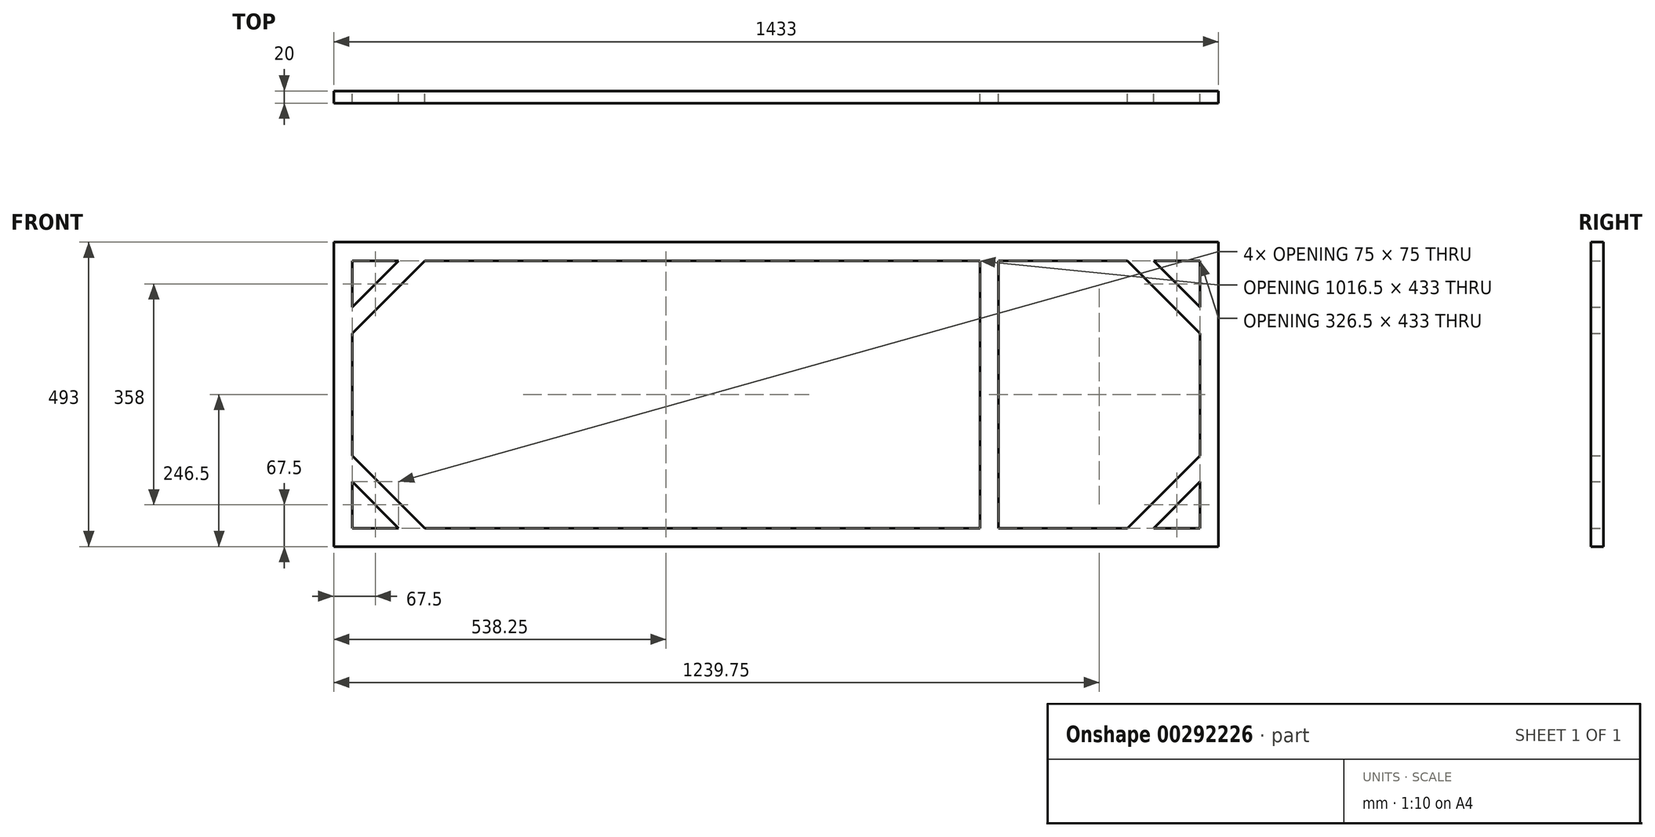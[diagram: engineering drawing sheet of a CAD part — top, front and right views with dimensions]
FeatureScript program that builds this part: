
annotation { "Feature Type Name" : "Feature", "Feature Type Description" : "" }
export const myFeature = defineFeature(function(context is Context, id is Id, definition is map)
    precondition{}
    {
        {
            var Q0;
            Q0=qCreatedBy(makeId("Front.planeOp"),FACE);
            var sketch = newSketch(context, id + "F0", { "sketchPlane" : qUnion([Q0])});
            skLineSegment(sketch, "E0.bottom", {"start": v(716.5, -246.5) * mm, "end": v(-716.5, -246.5) * mm});
            skLineSegment(sketch, "E0.top", {"start": v(716.5, 246.5) * mm, "end": v(-716.5, 246.5) * mm});
            skLineSegment(sketch, "E0.left", {"start": v(716.5, -246.5) * mm, "end": v(716.5, 246.5) * mm});
            skLineSegment(sketch, "E0.right", {"start": v(-716.5, -246.5) * mm, "end": v(-716.5, 246.5) * mm});
            skPoint(sketch, "E0.middle", {"position": v(0, 0) * mm});
            skLineSegment(sketch, "E1.0", {"start": v(686.5, 216.5) * mm, "end": v(611.5, 216.5) * mm});
            skLineSegment(sketch, "E1.1", {"start": v(686.5, -216.5) * mm, "end": v(686.5, -141.5) * mm});
            skLineSegment(sketch, "E1.2", {"start": v(686.5, -216.5) * mm, "end": v(611.5, -216.5) * mm});
            skLineSegment(sketch, "E1.3", {"start": v(-686.5, -216.5) * mm, "end": v(-686.5, -141.5) * mm});
            skLineSegment(sketch, "E2", {"start": v(330, 216.5) * mm, "end": v(330, -216.5) * mm});
            skLineSegment(sketch, "E3", {"start": v(360, -216.5) * mm, "end": v(360, 216.5) * mm});
            skLineSegment(sketch, "E4.trimOffspring", {"start": v(330, 216.5) * mm, "end": v(-569.07, 216.5) * mm});
            skLineSegment(sketch, "E5.trimOffspring", {"start": v(330, -216.5) * mm, "end": v(-569.07, -216.5) * mm});
            skLineSegment(sketch, "E6", {"start": v(-686.5, 141.5) * mm, "end": v(-611.5, 216.5) * mm});
            skLineSegment(sketch, "E7.0", {"start": v(-686.5, 99.07) * mm, "end": v(-569.07, 216.5) * mm});
            skLineSegment(sketch, "E8", {"start": v(-611.5, -216.5) * mm, "end": v(-686.5, -141.5) * mm});
            skLineSegment(sketch, "E9", {"start": v(611.5, -216.5) * mm, "end": v(686.5, -141.5) * mm});
            skLineSegment(sketch, "E10", {"start": v(686.5, 141.5) * mm, "end": v(611.5, 216.5) * mm});
            skLineSegment(sketch, "E11.0", {"start": v(-569.07, -216.5) * mm, "end": v(-686.5, -99.07) * mm});
            skLineSegment(sketch, "E12.0", {"start": v(569.07, -216.5) * mm, "end": v(686.5, -99.07) * mm});
            skLineSegment(sketch, "E13.0", {"start": v(686.5, 99.07) * mm, "end": v(569.07, 216.5) * mm});
            skLineSegment(sketch, "E14.trimOffspring", {"start": v(-611.5, 216.5) * mm, "end": v(-686.5, 216.5) * mm});
            skLineSegment(sketch, "E15.trimOffspring", {"start": v(-686.5, 141.5) * mm, "end": v(-686.5, 216.5) * mm});
            skLineSegment(sketch, "E16.trimOffspring", {"start": v(-686.5, -99.07) * mm, "end": v(-686.5, 99.07) * mm});
            skLineSegment(sketch, "E17.trimOffspring", {"start": v(-611.5, -216.5) * mm, "end": v(-686.5, -216.5) * mm});
            skLineSegment(sketch, "E18.trimOffspring", {"start": v(569.07, -216.5) * mm, "end": v(360, -216.5) * mm});
            skLineSegment(sketch, "E19.trimOffspring", {"start": v(686.5, -99.07) * mm, "end": v(686.5, 99.07) * mm});
            skLineSegment(sketch, "E20.trimOffspring", {"start": v(686.5, 141.5) * mm, "end": v(686.5, 216.5) * mm});
            skLineSegment(sketch, "E21.trimOffspring", {"start": v(569.07, 216.5) * mm, "end": v(360, 216.5) * mm});
            skSolve(sketch);
        }
        {
            var Q0;
            Q0 = qSketchRegion(id + "F0", true);
            extrude(context, id + "F1", {"entities" : qUnion([Q0]), "depth" : 20 * mm});
        }
    });
